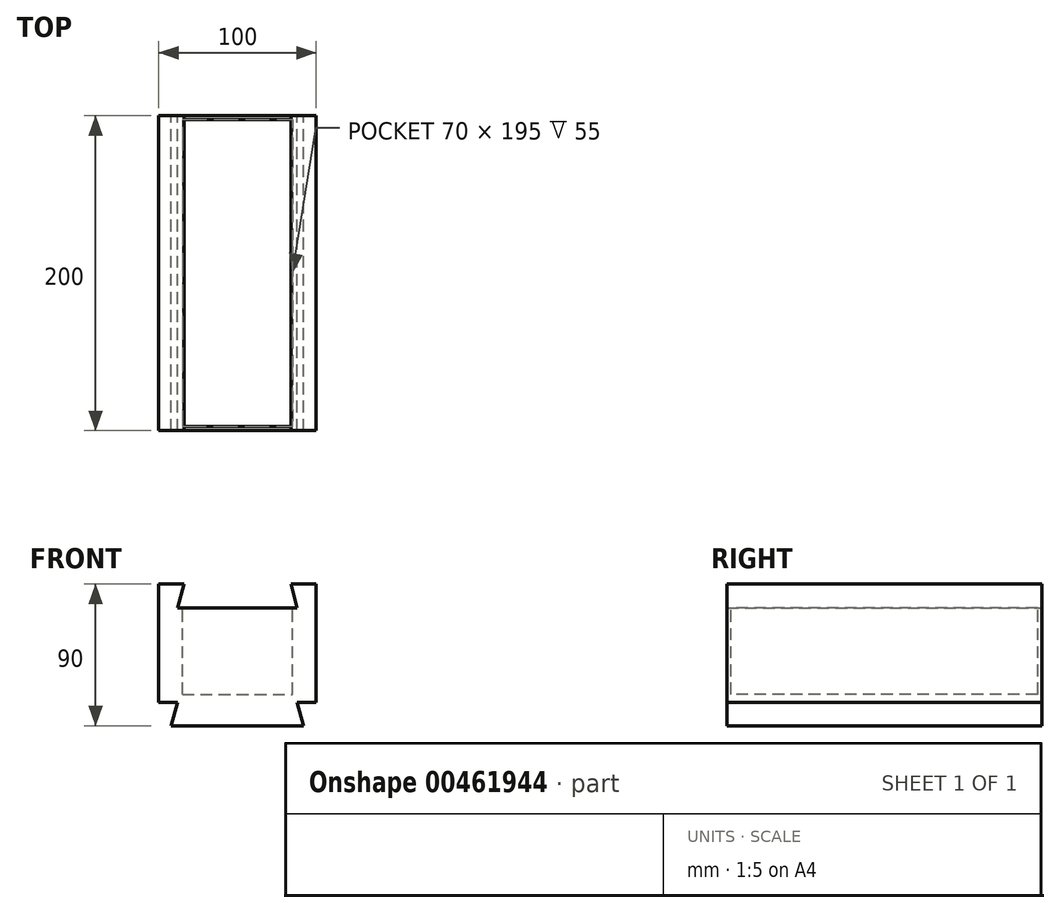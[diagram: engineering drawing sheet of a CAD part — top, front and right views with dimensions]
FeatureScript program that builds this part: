
annotation { "Feature Type Name" : "Feature", "Feature Type Description" : "" }
export const myFeature = defineFeature(function(context is Context, id is Id, definition is map)
    precondition{}
    {
        {
            var Q0;
            Q0=qCreatedBy(makeId("Front.planeOp"),FACE);
            var sketch = newSketch(context, id + "F0", { "sketchPlane" : qUnion([Q0])});
            skLineSegment(sketch, "E0.bottom", {"start": v(50, 30) * mm, "end": v(-50, 30) * mm});
            skLineSegment(sketch, "E0.top", {"start": v(50, -30) * mm, "end": v(-50, -30) * mm});
            skLineSegment(sketch, "E0.left", {"start": v(50, 30) * mm, "end": v(50, -30) * mm});
            skLineSegment(sketch, "E0.right", {"start": v(-50, 30) * mm, "end": v(-50, -30) * mm});
            skPoint(sketch, "E0.middle", {"position": v(0, 0) * mm});
            skLineSegment(sketch, "E1", {"start": v(-50, 30) * mm, "end": v(-50, 45) * mm});
            skLineSegment(sketch, "E2", {"start": v(-50, 45) * mm, "end": v(-34, 45) * mm});
            skLineSegment(sketch, "E3", {"start": v(-34, 45) * mm, "end": v(-38, 30) * mm});
            skLineSegment(sketch, "E4", {"start": v(50, 30) * mm, "end": v(50, 45) * mm});
            skLineSegment(sketch, "E5", {"start": v(50, 45) * mm, "end": v(34, 45) * mm});
            skLineSegment(sketch, "E6", {"start": v(34, 45) * mm, "end": v(38, 30) * mm});
            skLineSegment(sketch, "E7", {"start": v(-38, -30) * mm, "end": v(-42, -45) * mm});
            skLineSegment(sketch, "E8", {"start": v(-42, -45) * mm, "end": v(42, -45) * mm});
            skLineSegment(sketch, "E9", {"start": v(42, -45) * mm, "end": v(38, -30) * mm});
            skSolve(sketch);
        }
        {
            var Q0;
            Q0 = qSketchRegion(id + "F0", true);
            extrude(context, id + "F1", {"entities" : qUnion([Q0]), "endBound" : BoundingType.SYMMETRIC, "depth" : 200 * mm});
        }
        {
            var Q0;
            Q0=qCreatedBy(makeId("Front.planeOp"),FACE);
            var sketch = newSketch(context, id + "F2", { "sketchPlane" : qUnion([Q0])});
            skPoint(sketch, "E10.middle", {"position": v(0, 0) * mm});
            skLineSegment(sketch, "E11.bottom", {"start": v(-35, -25) * mm, "end": v(35, -25) * mm});
            skLineSegment(sketch, "E11.top", {"start": v(-35, 30) * mm, "end": v(35, 30) * mm});
            skLineSegment(sketch, "E11.left", {"start": v(-35, -25) * mm, "end": v(-35, 30) * mm});
            skLineSegment(sketch, "E11.right", {"start": v(35, -25) * mm, "end": v(35, 30) * mm});
            skSolve(sketch);
        }
        {
            var Q0;
            Q0 = qSketchRegion(id + "F2", true);
            extrude(context, id + "F3", {"entities" : qUnion([Q0]), "operationType" : NewBodyOperationType.REMOVE, "endBound" : BoundingType.SYMMETRIC, "oppositeDirection" : true, "depth" : 195 * mm});
        }
    });
